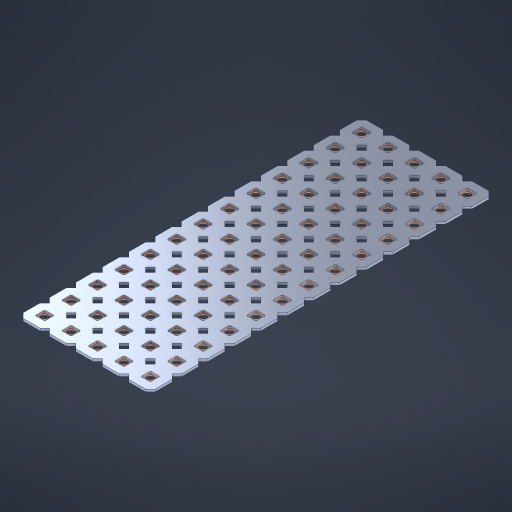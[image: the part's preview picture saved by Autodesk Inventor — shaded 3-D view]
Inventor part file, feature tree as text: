
AUTODESK INVENTOR PART (.ipt)
format: ipt  version: 2023 (Build 270158000, 158)  size: 1,014,784 bytes
history: native  units: in
note: dims shown in document units (in); Inventor stores cm internally (conversion verified against a paired STEP export)
features: other x66, extrude x64, sketch x2, pattern_linear x1
ambient origin geometry x8: Origin, YZ Plane, XZ Plane, XY Plane, X Axis, Y Axis, Z Axis, Center Point
bodies: Solid1 (feature_tree), Body (feature_tree)
feature tree (133):
  pattern_linear  "Rectangular Pattern1"  Spacing1=0.09in  [1 undecoded]
  sketch  "Sketch1"  dims[d1=0.5in]
  sketch  "Sketch2"  dims[d2=0.182in d3=0.09in d4=0.09in d5=0.09in d6=0.09in d7=0.09in d8=0.09in d9=0.09in d10=0.09in d11=0.02in d13=0.0in d14=0.172in d15=0.0625in d16=0.0in d19=0.5in d22=0.5in]
  other  "Srf1"
  other  "Srf126"
  other  "Srf127"
  other  "Srf128"
  other  "Srf129"
  other  "Srf130"
  other  "Srf131"
  other  "Srf250"
  other  "Srf251"
  other  "Srf252"
  other  "Srf253"
  other  "Srf254"
  other  "Srf255"
  other  "Srf268"
  other  "Srf269"
  other  "Srf270"
  other  "Srf271"
  other  "Srf272"
  other  "Srf273"
  other  "Srf274"
  other  "Srf275"
  other  "Srf276"
  other  "Srf277"
  other  "Srf278"
  other  "Srf279"
  other  "Srf280"
  other  "Srf293"
  other  "Srf294"
  other  "Srf295"
  other  "Srf296"
  other  "Srf297"
  other  "Srf298"
  other  "Srf299"
  other  "Srf300"
  other  "Srf301"
  other  "Srf302"
  other  "Srf303"
  other  "Srf304"
  other  "Srf305"
  other  "Srf318"
  other  "Srf319"
  other  "Srf320"
  other  "Srf321"
  other  "Srf322"
  other  "Srf323"
  other  "Srf324"
  other  "Srf325"
  other  "Srf326"
  other  "Srf327"
  other  "Srf328"
  other  "Srf329"
  other  "Srf330"
  other  "Srf343"
  other  "Srf344"
  other  "Srf345"
  other  "Srf346"
  other  "Srf347"
  other  "Srf348"
  other  "Srf349"
  other  "Srf350"
  other  "Srf351"
  other  "Srf352"
  other  "Srf353"
  other  "Srf354"
  other  "Srf355"
  other  "Circle"
  extrude  "ExtrusionSrf126"  Depth=0.09in
  extrude  "ExtrusionSrf127"  Depth=0.09in
  extrude  "ExtrusionSrf128"  Depth=0.09in
  extrude  "ExtrusionSrf129"  Depth=0.09in
  extrude  "ExtrusionSrf130"  Depth=0.09in
  extrude  "ExtrusionSrf131"  Depth=0.09in
  extrude  "ExtrusionSrf250"  Depth=0.09in
  extrude  "ExtrusionSrf251"  Depth=0.02in
  extrude  "ExtrusionSrf252"  TaperAngle=0.0deg  [1 undecoded]
  extrude  "ExtrusionSrf253"  Depth=0.5in
  extrude  "ExtrusionSrf254"  Depth=0.5in TaperAngle=0.0deg
  extrude  "ExtrusionSrf255"  Depth=0.5in
  extrude  "ExtrusionSrf268"  Depth=0.5in
  extrude  "ExtrusionSrf269"  [1 undecoded]
  extrude  "ExtrusionSrf270"  [1 undecoded]
  extrude  "ExtrusionSrf271"  [1 undecoded]
  extrude  "ExtrusionSrf272"  [1 undecoded]
  extrude  "ExtrusionSrf273"  [1 undecoded]
  extrude  "ExtrusionSrf274"  [1 undecoded]
  extrude  "ExtrusionSrf275"  [1 undecoded]
  extrude  "ExtrusionSrf276"  [1 undecoded]
  extrude  "ExtrusionSrf277"  [1 undecoded]
  extrude  "ExtrusionSrf278"  [1 undecoded]
  extrude  "ExtrusionSrf279"  [1 undecoded]
  extrude  "ExtrusionSrf280"  [1 undecoded]
  extrude  "ExtrusionSrf293"  [1 undecoded]
  extrude  "ExtrusionSrf294"  [1 undecoded]
  extrude  "ExtrusionSrf295"  [1 undecoded]
  extrude  "ExtrusionSrf296"  [1 undecoded]
  extrude  "ExtrusionSrf297"  [1 undecoded]
  extrude  "ExtrusionSrf298"  [1 undecoded]
  extrude  "ExtrusionSrf299"  [1 undecoded]
  extrude  "ExtrusionSrf300"  [1 undecoded]
  extrude  "ExtrusionSrf301"  [1 undecoded]
  extrude  "ExtrusionSrf302"  [1 undecoded]
  extrude  "ExtrusionSrf303"  [1 undecoded]
  extrude  "ExtrusionSrf304"  [1 undecoded]
  extrude  "ExtrusionSrf305"  [1 undecoded]
  extrude  "ExtrusionSrf318"  [1 undecoded]
  extrude  "ExtrusionSrf319"  [1 undecoded]
  extrude  "ExtrusionSrf320"  [1 undecoded]
  extrude  "ExtrusionSrf321"  [1 undecoded]
  extrude  "ExtrusionSrf322"  [1 undecoded]
  extrude  "ExtrusionSrf323"  [1 undecoded]
  extrude  "ExtrusionSrf324"  [1 undecoded]
  extrude  "ExtrusionSrf325"  [1 undecoded]
  extrude  "ExtrusionSrf326"  [1 undecoded]
  extrude  "ExtrusionSrf327"  [1 undecoded]
  extrude  "ExtrusionSrf328"  [1 undecoded]
  extrude  "ExtrusionSrf329"  [1 undecoded]
  extrude  "ExtrusionSrf330"  [1 undecoded]
  extrude  "ExtrusionSrf343"  [1 undecoded]
  extrude  "ExtrusionSrf344"  [1 undecoded]
  extrude  "ExtrusionSrf345"  [1 undecoded]
  extrude  "ExtrusionSrf346"  [1 undecoded]
  extrude  "ExtrusionSrf347"  [1 undecoded]
  extrude  "ExtrusionSrf348"  [1 undecoded]
  extrude  "ExtrusionSrf349"  [1 undecoded]
  extrude  "ExtrusionSrf350"  [1 undecoded]
  extrude  "ExtrusionSrf351"  [1 undecoded]
  extrude  "ExtrusionSrf352"  [1 undecoded]
  extrude  "ExtrusionSrf353"  [1 undecoded]
  extrude  "ExtrusionSrf354"  [1 undecoded]
  extrude  "ExtrusionSrf355"  [1 undecoded]
note: 53 required parameter values undecoded (feature->parameter linkage not recoverable at this tier; creation-order binding heuristic only, values carry confidence <= 0.55)
